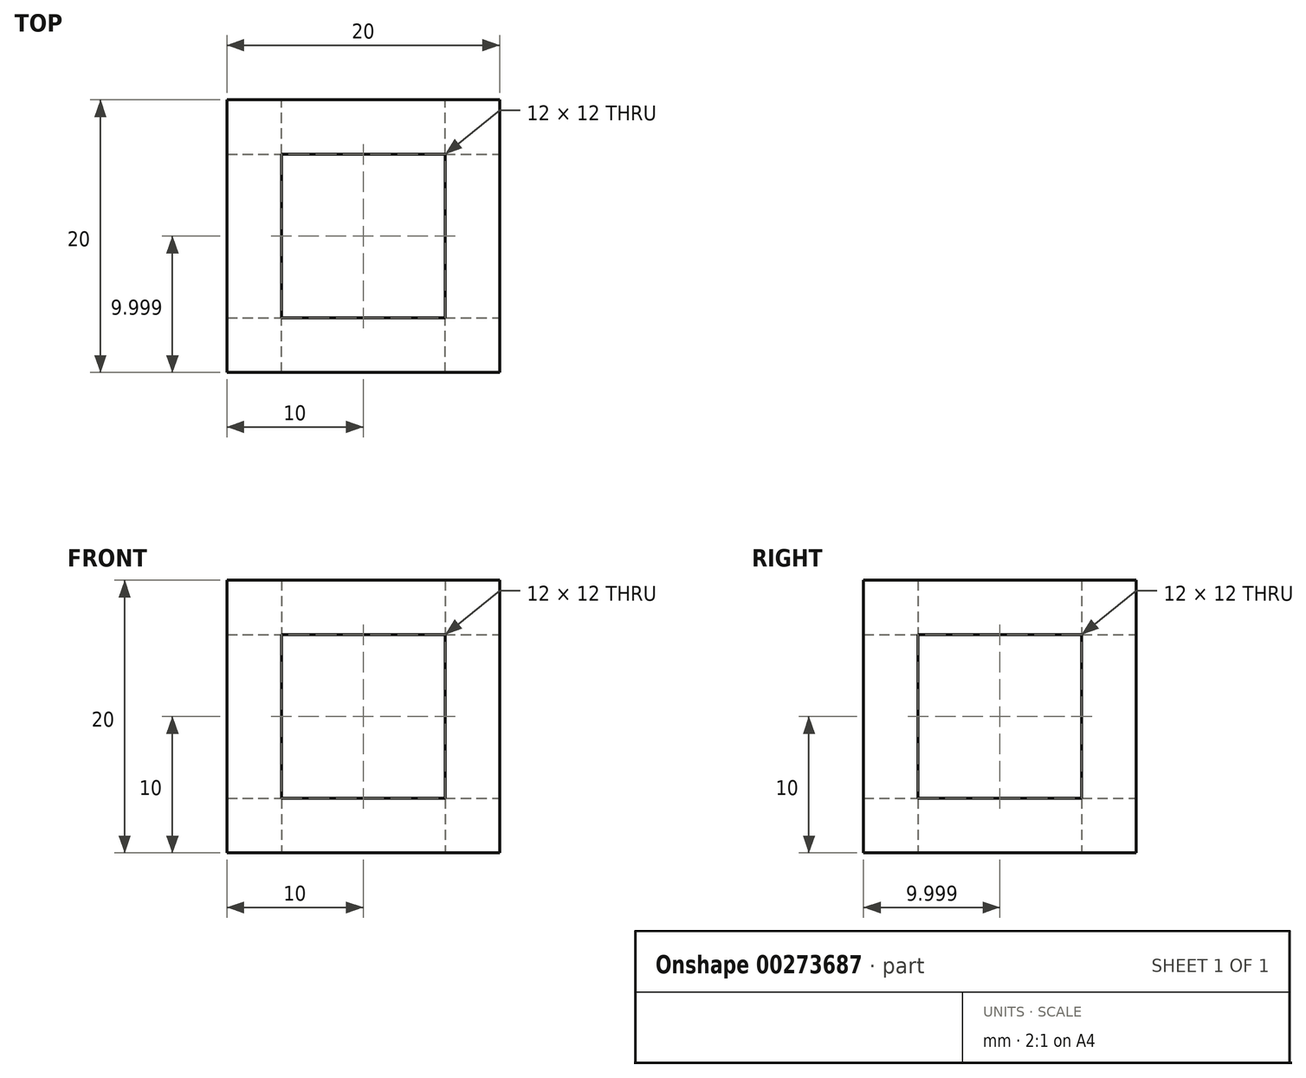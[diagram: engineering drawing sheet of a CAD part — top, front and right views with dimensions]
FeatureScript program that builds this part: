
annotation { "Feature Type Name" : "Feature", "Feature Type Description" : "" }
export const myFeature = defineFeature(function(context is Context, id is Id, definition is map)
    precondition{}
    {
        {
            var Q0;
            Q0=qCreatedBy(makeId("Top.planeOp"),FACE);
            var sketch = newSketch(context, id + "F0", { "sketchPlane" : qUnion([Q0])});
            skLineSegment(sketch, "E0.bottom", {"start": v(-51.3, -13.3) * mm, "end": v(-31.3, -13.3) * mm});
            skLineSegment(sketch, "E0.top", {"start": v(-51.3, -33.3) * mm, "end": v(-31.3, -33.3) * mm});
            skLineSegment(sketch, "E0.left", {"start": v(-51.3, -13.3) * mm, "end": v(-51.3, -33.3) * mm});
            skLineSegment(sketch, "E0.right", {"start": v(-31.3, -13.3) * mm, "end": v(-31.3, -33.3) * mm});
            skSolve(sketch);
        }
        {
            var Q0;
            Q0 = qSketchRegion(id + "F0", true);
            extrude(context, id + "F1", {"entities" : qUnion([Q0]), "depth" : 20 * mm});
        }
        {
            var Q0;
            Q0=qCreatedBy(makeId("Right.planeOp"),FACE);
            var sketch = newSketch(context, id + "F2", { "sketchPlane" : qUnion([Q0])});
            skLineSegment(sketch, "E1.bottom", {"start": v(-29.3, 16) * mm, "end": v(-17.3, 16) * mm});
            skLineSegment(sketch, "E1.top", {"start": v(-29.3, 4) * mm, "end": v(-17.3, 4) * mm});
            skLineSegment(sketch, "E1.left", {"start": v(-29.3, 16) * mm, "end": v(-29.3, 4) * mm});
            skLineSegment(sketch, "E1.right", {"start": v(-17.3, 16) * mm, "end": v(-17.3, 4) * mm});
            skSolve(sketch);
        }
        {
            var Q0;
            Q0 = qSketchRegion(id + "F2", true);
            extrude(context, id + "F3", {"entities" : qUnion([Q0]), "operationType" : NewBodyOperationType.REMOVE, "oppositeDirection" : true, "depth" : 90 * mm});
        }
        {
            var Q0;
            Q0=qCreatedBy(makeId("Front.planeOp"),FACE);
            var sketch = newSketch(context, id + "F4", { "sketchPlane" : qUnion([Q0])});
            skLineSegment(sketch, "E2.bottom", {"start": v(-47.3, 16) * mm, "end": v(-35.3, 16) * mm});
            skLineSegment(sketch, "E2.top", {"start": v(-47.3, 4) * mm, "end": v(-35.3, 4) * mm});
            skLineSegment(sketch, "E2.left", {"start": v(-47.3, 16) * mm, "end": v(-47.3, 4) * mm});
            skLineSegment(sketch, "E2.right", {"start": v(-35.3, 16) * mm, "end": v(-35.3, 4) * mm});
            skSolve(sketch);
        }
        {
            var Q0;
            Q0=makeQuery(id+"F4.imprint","IMPRINT",FACE,{"disambiguationData":[TD([[makeQuery(id+"F4.imprint","IMPRINT",EDGE,{"derivedFrom":sQuery(id+"F4.wireOp",EDGE,"E2.bottom")}),-1.0]])]});
            extrude(context, id + "F5", {"entities" : qUnion([Q0]), "operationType" : NewBodyOperationType.REMOVE, "depth" : 60.3 * mm});
        }
        {
            var Q0;
            Q0=qCreatedBy(makeId("Top.planeOp"),FACE);
            var sketch = newSketch(context, id + "F6", { "sketchPlane" : qUnion([Q0])});
            skLineSegment(sketch, "E3.bottom", {"start": v(-47.3, -17.3) * mm, "end": v(-35.3, -17.3) * mm});
            skLineSegment(sketch, "E3.top", {"start": v(-47.3, -29.3) * mm, "end": v(-35.3, -29.3) * mm});
            skLineSegment(sketch, "E3.left", {"start": v(-47.3, -17.3) * mm, "end": v(-47.3, -29.3) * mm});
            skLineSegment(sketch, "E3.right", {"start": v(-35.3, -17.3) * mm, "end": v(-35.3, -29.3) * mm});
            skSolve(sketch);
        }
        {
            var Q0;
            Q0 = qSketchRegion(id + "F6", true);
            extrude(context, id + "F7", {"entities" : qUnion([Q0]), "operationType" : NewBodyOperationType.REMOVE, "depth" : 36 * mm});
        }
    });
